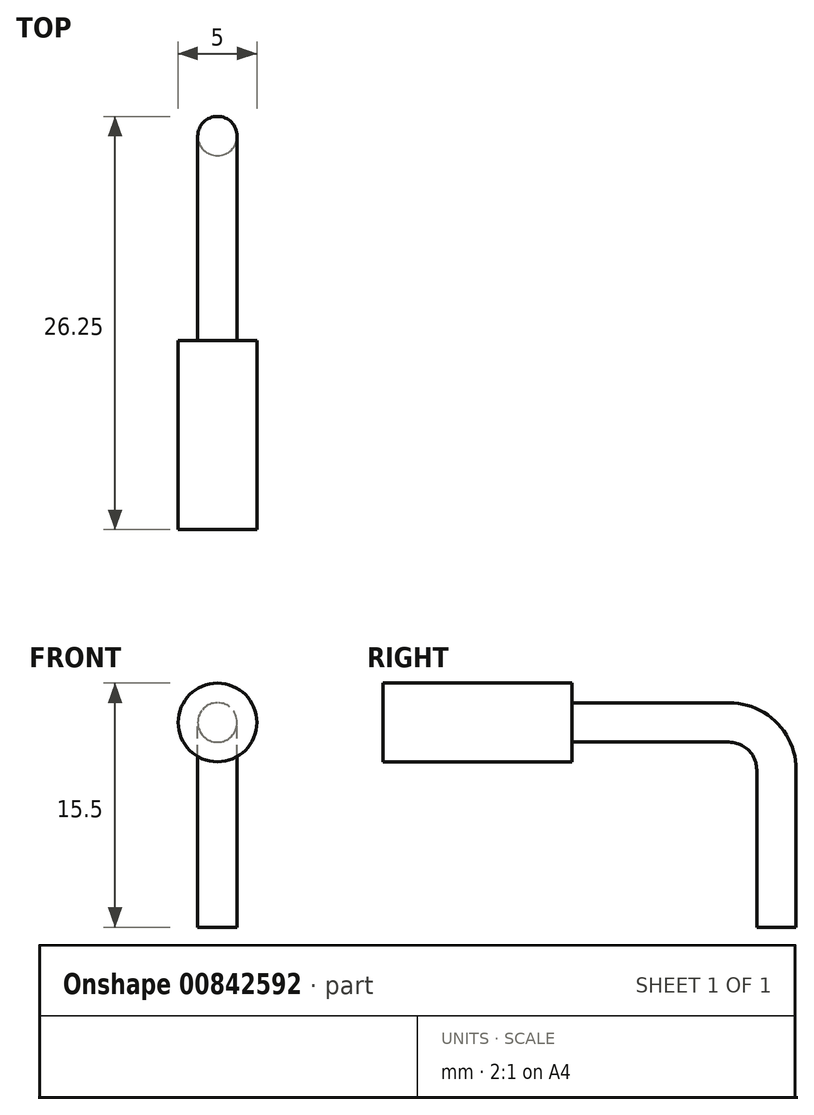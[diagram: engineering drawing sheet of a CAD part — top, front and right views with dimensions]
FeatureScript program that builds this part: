
annotation { "Feature Type Name" : "Feature", "Feature Type Description" : "" }
export const myFeature = defineFeature(function(context is Context, id is Id, definition is map)
    precondition{}
    {
        {
            var Q0;
            Q0=qCreatedBy(makeId("Front.planeOp"),FACE);
            var sketch = newSketch(context, id + "F0", { "sketchPlane" : qUnion([Q0])});
            skCircle(sketch, "E0", {"center": v(0, 0) * mm, "radius": 2.5 * mm});
            skSolve(sketch);
        }
        {
            var Q0;
            Q0 = qSketchRegion(id + "F0", true);
            extrude(context, id + "F1", {"entities" : qUnion([Q0]), "oppositeDirection" : true, "depth" : 12 * mm, "offsetDistance" : 25 * mm});
        }
        {
            var Q0;
            Q0=qCreatedBy(makeId("Right.planeOp"),FACE);
            var sketch = newSketch(context, id + "F2", { "sketchPlane" : qUnion([Q0])});
            skLineSegment(sketch, "E1", {"start": v(12, 0) * mm, "end": v(22, 0) * mm});
            skArc(sketch, "E2", {"start": v(25, -3) * mm, "mid": v(24.12, -0.88) * mm, "end": v(22, 0) * mm});
            skLineSegment(sketch, "E3", {"start": v(25, -3) * mm, "end": v(25, -13) * mm});
            skSolve(sketch);
        }
        {
            var Q0;
            Q0=makeQuery(id+"F1.opExtrude","CAP_FACE",FACE,{"disambiguationData":[OSD([sQuery(id+"F0.wireOp",EDGE,"E0")])],"isStart":false});
            var sketch = newSketch(context, id + "F3", { "sketchPlane" : qUnion([Q0])});
            skCircle(sketch, "E4", {"center": v(0, 0) * mm, "radius": 1.25 * mm});
            skSolve(sketch);
        }
        {
            var Q0;
            Q0 = qSketchRegion(id + "F3", true);
            var Q1;
            Q1 = qConstructionFilter(qBodyType(qCreatedBy(id + "F2" ,EDGE), BodyType.WIRE), ConstructionObject.NO);
            sweep(context, id + "F4", {"operationType" : NewBodyOperationType.ADD, "profiles" : qUnion([Q0]), "path" : qUnion([Q1])});
        }
    });
